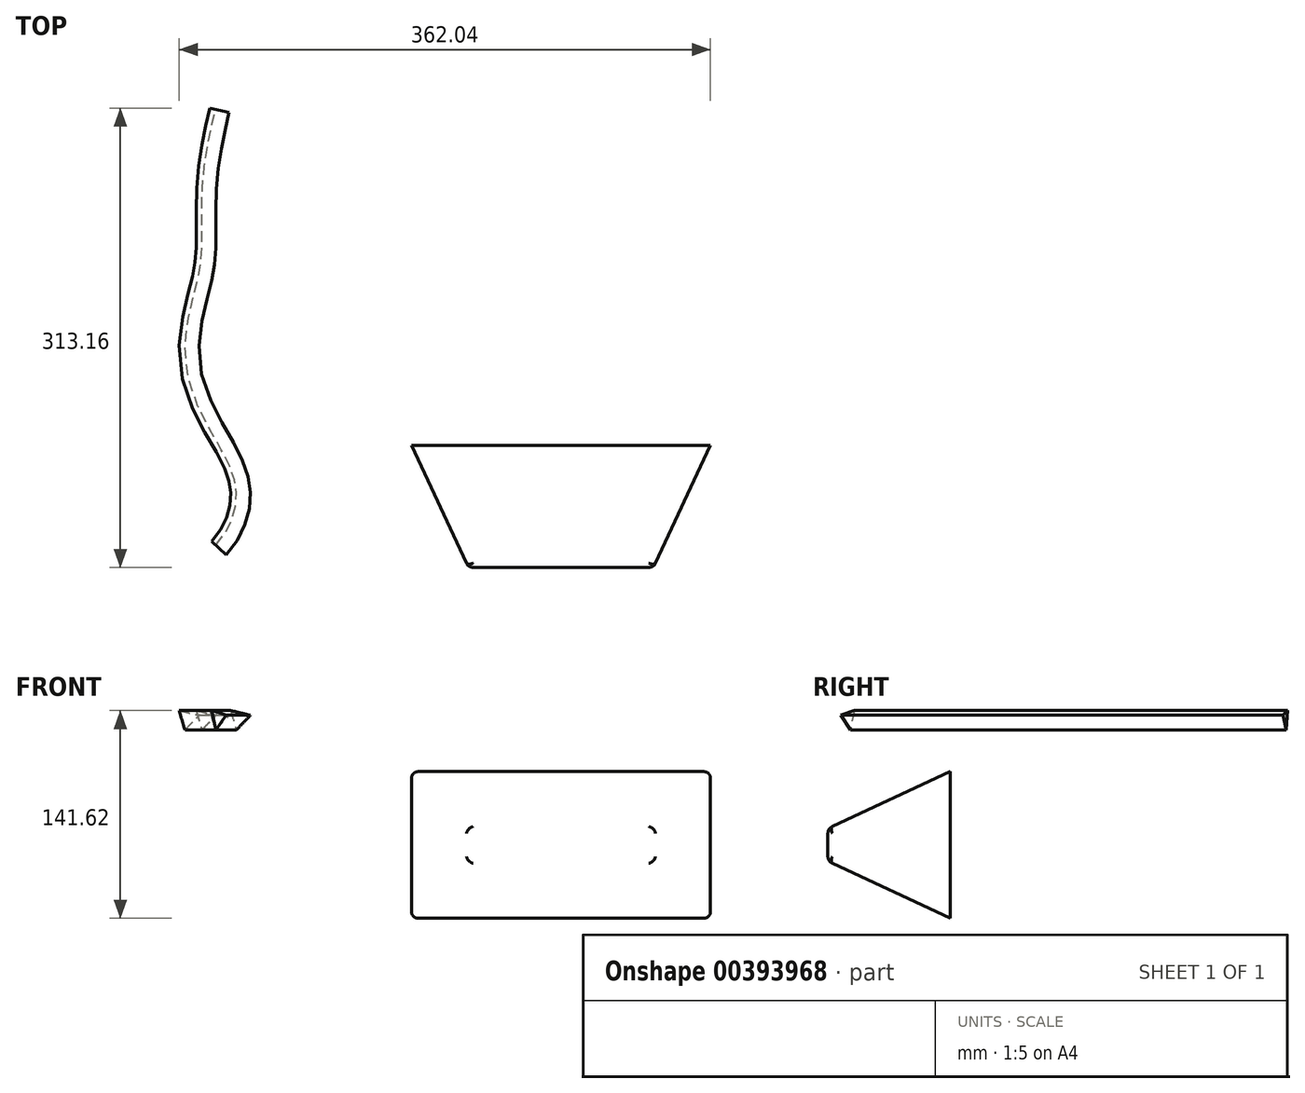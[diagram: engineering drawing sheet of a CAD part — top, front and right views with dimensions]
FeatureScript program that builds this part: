
annotation { "Feature Type Name" : "Feature", "Feature Type Description" : "" }
export const myFeature = defineFeature(function(context is Context, id is Id, definition is map)
    precondition{}
    {
        {
            var Q0;
            Q0=qCreatedBy(makeId("Top.planeOp"),FACE);
            var sketch = newSketch(context, id + "F0", { "sketchPlane" : qUnion([Q0])});
            skFitSpline(sketch, "E0", {"points": [v(-72.96, -90.95) * mm, v(-52.7, -13.67) * mm, v(-84.25, 55.8) * mm, v(-75.33, 114.42) * mm, v(-73.29, 172.62) * mm, v(-65.16, 221.52) * mm], "startDerivative": vector(272.66, 292.99) * mm, "endDerivative": vector(61.14, 268.32) * mm});
            skSolve(sketch);
        }
        {
            var Q0;
            Q0=sQuery(id+"F0.wireOp",EDGE,"E0");
            var Q1;
            Q1=sQuery(id+"F0.wireOp",VERTEX,"E0.start");
            cPlane(context, id + "F1", {"entities" : qUnion([Q0, Q1]), "cplaneType" : CPlaneType.CURVE_POINT, "offset" : 25.4 * mm, "width" : 152.4 * mm, "height" : 152.4 * mm});
        }
        {
            var Q0;
            Q0=qCreatedBy(id+"F1.planeOp",FACE);
            var sketch = newSketch(context, id + "F2", { "sketchPlane" : qUnion([Q0])});
            skCircle(sketch, "E1.cCircle", {"center": v(23.18, -2.26) * mm, "radius": 4 * mm, "construction": true});
            skLineSegment(sketch, "E1.0", {"start": v(25.06, -10.03) * mm, "end": v(15.5, 0) * mm});
            skLineSegment(sketch, "E1.1", {"start": v(15.5, 0) * mm, "end": v(28.97, 3.26) * mm});
            skLineSegment(sketch, "E1.2", {"start": v(28.97, 3.26) * mm, "end": v(25.06, -10.03) * mm});
            skPoint(sketch, "E1.0.midPoint", {"position": v(20.29, -5.01) * mm});
            skSolve(sketch);
        }
        {
            var Q0;
            Q0=makeQuery(id+"F2.imprint","IMPRINT",FACE,{"disambiguationData":[TD([[makeQuery(id+"F2.imprint","IMPRINT",EDGE,{"derivedFrom":sQuery(id+"F2.wireOp",EDGE,"E1.0")}),-1.0]])]});
            var Q1;
            Q1=sQuery(id+"F0.wireOp",EDGE,"E0");
            sweep(context, id + "F3", {"profiles" : qUnion([Q0]), "path" : qUnion([Q1])});
        }
        {
            var Q0;
            Q0=qCreatedBy(makeId("Front.planeOp"),FACE);
            var sketch = newSketch(context, id + "F4", { "sketchPlane" : qUnion([Q0])});
            skLineSegment(sketch, "E2.bottom", {"start": v(35.73, -38.38) * mm, "end": v(239.43, -38.38) * mm});
            skLineSegment(sketch, "E2.top", {"start": v(35.73, -138.36) * mm, "end": v(239.43, -138.36) * mm});
            skLineSegment(sketch, "E2.left", {"start": v(35.73, -38.38) * mm, "end": v(35.73, -138.36) * mm});
            skLineSegment(sketch, "E2.right", {"start": v(239.43, -38.38) * mm, "end": v(239.43, -138.36) * mm});
            skSolve(sketch);
        }
        {
            var Q0;
            Q0=makeQuery(id+"F4.imprint","IMPRINT",FACE,{"disambiguationData":[TD([[makeQuery(id+"F4.imprint","IMPRINT",EDGE,{"derivedFrom":sQuery(id+"F4.wireOp",EDGE,"E2.bottom")}),-1.0]])]});
            extrude(context, id + "F5", {"entities" : qUnion([Q0]), "depth" : 83.31 * mm, "hasDraft" : true, "draftAngle" : 25 * degree, "draftPullDirection" : true});
        }
        {
            var Q0;
            Q0=makeQuery(id+"F5.opExtrude","SWEPT_EDGE",EDGE,{"disambiguationData":[OSD([sQuery(id+"F4.wireOp",EDGE,"E2.top"),sQuery(id+"F4.wireOp",EDGE,"E2.right")])]});
            var Q1;
            Q1=makeQuery(id+"F5.opExtrude","SWEPT_EDGE",EDGE,{"disambiguationData":[OSD([sQuery(id+"F4.wireOp",EDGE,"E2.bottom"),sQuery(id+"F4.wireOp",EDGE,"E2.right")])]});
            var Q2;
            Q2=makeQuery(id+"F5.opExtrude","SWEPT_EDGE",EDGE,{"disambiguationData":[OSD([sQuery(id+"F4.wireOp",EDGE,"E2.top"),sQuery(id+"F4.wireOp",EDGE,"E2.left")])]});
            var Q3;
            Q3=makeQuery(id+"F5.opExtrude","SWEPT_EDGE",EDGE,{"disambiguationData":[OSD([sQuery(id+"F4.wireOp",EDGE,"E2.bottom"),sQuery(id+"F4.wireOp",EDGE,"E2.left")])]});
            var Q4;
            Q4=makeQuery(id+"F5.opExtrude","CAP_FACE",FACE,{"disambiguationData":[OSD([sQuery(id+"F4.wireOp",EDGE,"E2.bottom"),sQuery(id+"F4.wireOp",EDGE,"E2.top"),sQuery(id+"F4.wireOp",EDGE,"E2.left"),sQuery(id+"F4.wireOp",EDGE,"E2.right")])],"isStart":false});
            fillet(context, id + "F6", {"entities" : qUnion([Q0, Q1, Q2, Q3, Q4]), "radius" : 5.08 * mm, "tangentPropagation" : true, "allowEdgeOverflow" : false});
        }
    });
